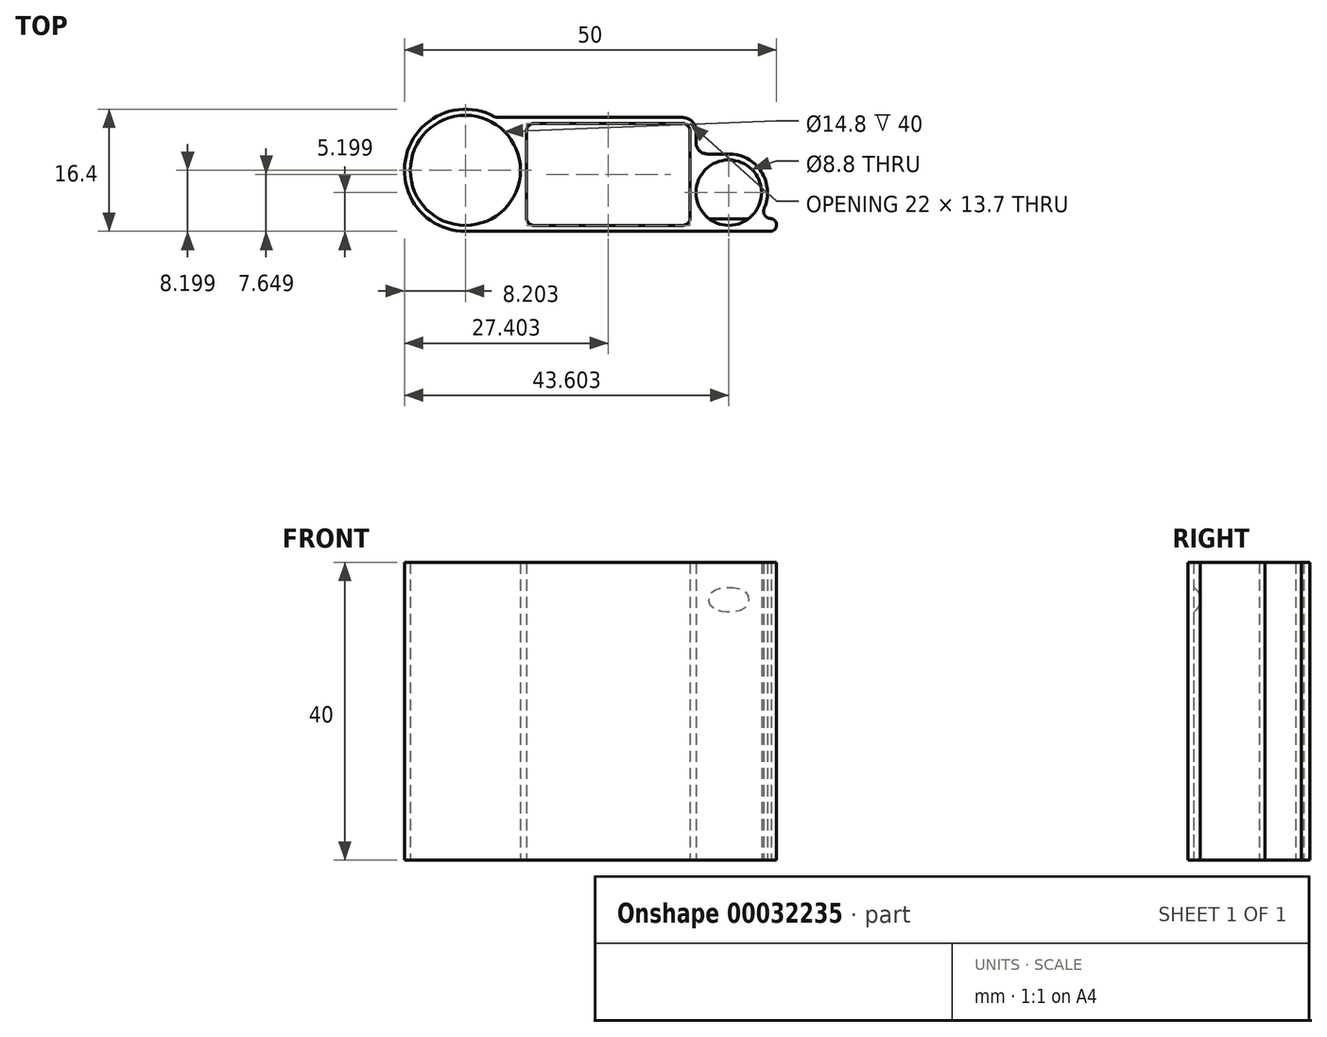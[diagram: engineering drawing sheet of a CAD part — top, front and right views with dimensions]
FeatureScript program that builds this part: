
annotation { "Feature Type Name" : "Feature", "Feature Type Description" : "" }
export const myFeature = defineFeature(function(context is Context, id is Id, definition is map)
    precondition{}
    {
        {
            var Q0;
            Q0=qCreatedBy(makeId("Top.planeOp"),FACE);
            var sketch = newSketch(context, id + "F0", { "sketchPlane" : qUnion([Q0])});
            skCircle(sketch, "E0", {"center": v(-31.66, -11.88) * mm, "radius": 7.4 * mm});
            skLineSegment(sketch, "E1.0", {"start": v(-31.66, -20.08) * mm, "end": v(9.34, -20.08) * mm});
            skArc(sketch, "E2.trimOffspring", {"start": v(-27.77, -4.66) * mm, "mid": v(-39.6, -9.88) * mm, "end": v(-31.66, -20.08) * mm});
            skPoint(sketch, "E3.end.orphan", {"position": v(-39.86, -11.88) * mm});
            skPoint(sketch, "E4.visualSharp", {"position": v(10.14, -20.08) * mm});
            skPoint(sketch, "E5.visualSharp", {"position": v(0.2, -18.37) * mm});
            skLineSegment(sketch, "E6", {"start": v(10.14, -19.17) * mm, "end": v(10.14, -19.28) * mm});
            skArc(sketch, "E7.filletArc", {"start": v(10.14, -19.17) * mm, "mid": v(9.94, -18.64) * mm, "end": v(9.43, -18.38) * mm});
            skArc(sketch, "E8.filletArc", {"start": v(9.34, -20.08) * mm, "mid": v(9.9, -19.85) * mm, "end": v(10.14, -19.28) * mm});
            skLineSegment(sketch, "E9", {"start": v(-23.46, -18.28) * mm, "end": v(-23.46, -6.58) * mm});
            skLineSegment(sketch, "E10", {"start": v(-22.46, -19.28) * mm, "end": v(-2.46, -19.28) * mm});
            skLineSegment(sketch, "E11", {"start": v(-22.46, -5.58) * mm, "end": v(-2.46, -5.58) * mm});
            skLineSegment(sketch, "E12.trimOffspring", {"start": v(-1.46, -6.58) * mm, "end": v(-1.46, -18.28) * mm});
            skCircle(sketch, "E13", {"center": v(3.74, -14.88) * mm, "radius": 4.4 * mm});
            skArc(sketch, "E14", {"start": v(8.5, -16.97) * mm, "mid": v(8.1, -12.04) * mm, "end": v(3.74, -9.68) * mm});
            skPoint(sketch, "E15.visualSharp", {"position": v(-23.82, -9.48) * mm});
            skPoint(sketch, "E16.visualSharp", {"position": v(9.34, -18.37) * mm});
            skPoint(sketch, "E17.visualSharp", {"position": v(7.6, -18.37) * mm});
            skArc(sketch, "E17.filletArc", {"start": v(8.5, -16.97) * mm, "mid": v(8.58, -17.92) * mm, "end": v(9.42, -18.37) * mm});
            skPoint(sketch, "E18.visualSharp", {"position": v(-23.46, -5.58) * mm});
            skArc(sketch, "E18.filletArc", {"start": v(-22.46, -5.58) * mm, "mid": v(-23.16, -5.87) * mm, "end": v(-23.46, -6.58) * mm});
            skPoint(sketch, "E19.visualSharp", {"position": v(-23.46, -19.28) * mm});
            skArc(sketch, "E19.filletArc", {"start": v(-23.46, -18.28) * mm, "mid": v(-23.16, -18.99) * mm, "end": v(-22.46, -19.28) * mm});
            skPoint(sketch, "E20.visualSharp", {"position": v(-1.46, -5.58) * mm});
            skArc(sketch, "E20.filletArc", {"start": v(-1.46, -6.58) * mm, "mid": v(-1.75, -5.87) * mm, "end": v(-2.46, -5.58) * mm});
            skPoint(sketch, "E21.visualSharp", {"position": v(-1.46, -19.28) * mm});
            skArc(sketch, "E21.filletArc", {"start": v(-2.46, -19.28) * mm, "mid": v(-1.75, -18.99) * mm, "end": v(-1.46, -18.28) * mm});
            skLineSegment(sketch, "E22.0", {"start": v(-27.3, -4.78) * mm, "end": v(-2.46, -4.78) * mm});
            skPoint(sketch, "E23.visualSharp", {"position": v(-27.55, -4.78) * mm});
            skArc(sketch, "E23.filletArc", {"start": v(-27.77, -4.66) * mm, "mid": v(-27.54, -4.75) * mm, "end": v(-27.3, -4.78) * mm});
            skArc(sketch, "E24.0", {"start": v(-0.66, -6.58) * mm, "mid": v(-1.18, -5.3) * mm, "end": v(-2.46, -4.78) * mm});
            skLineSegment(sketch, "E25.0", {"start": v(-0.66, -6.58) * mm, "end": v(-0.66, -8.18) * mm});
            skLineSegment(sketch, "E26", {"start": v(3.74, -9.68) * mm, "end": v(0.84, -9.68) * mm});
            skPoint(sketch, "E27.visualSharp", {"position": v(-0.66, -9.68) * mm});
            skArc(sketch, "E27.filletArc", {"start": v(-0.66, -8.18) * mm, "mid": v(-0.22, -9.24) * mm, "end": v(0.84, -9.68) * mm});
            skLineSegment(sketch, "E28", {"start": v(9.42, -18.37) * mm, "end": v(9.43, -18.38) * mm});
            skSolve(sketch);
        }
        {
            var Q0;
            Q0=makeQuery(id+"F0.imprint","IMPRINT",FACE,{"disambiguationData":[TD([[makeQuery(id+"F0.imprint","IMPRINT",EDGE,{"derivedFrom":sQuery(id+"F0.wireOp",EDGE,"E0")}),-1.0]])]});
            var Q1;
            Q1=qSketchRegion(id+"F0",true);
            extrude(context, id + "F1", {"entities" : qUnion([Q0, Q1]), "depth" : 40 * mm});
        }
        {
            var Q0;
            Q0=qCreatedBy(makeId("Right.planeOp"),FACE);
            cPlane(context, id + "F2", {"entities" : qUnion([Q0]), "cplaneType" : CPlaneType.OFFSET, "offset" : 7 * mm, "width" : 150 * mm, "height" : 150 * mm});
        }
        {
            var Q0;
            Q0=qCreatedBy(id+"F2.planeOp",FACE);
            var sketch = newSketch(context, id + "F3", { "sketchPlane" : qUnion([Q0])});
            skArc(sketch, "E29", {"start": v(-19.58, 33.17) * mm, "mid": v(-18.38, 35) * mm, "end": v(-19.58, 36.83) * mm});
            skLineSegment(sketch, "E30", {"start": v(-20.38, 35) * mm, "end": v(-18.38, 35) * mm});
            skLineSegment(sketch, "E31", {"start": v(-19.58, 36.83) * mm, "end": v(-19.58, 33.17) * mm});
            skSolve(sketch);
        }
        {
            var Q0;
            Q0=qSketchRegion(id+"F3",true);
            extrude(context, id + "F4", {"entities" : qUnion([Q0]), "operationType" : NewBodyOperationType.ADD, "oppositeDirection" : true, "depth" : 8 * mm});
        }
    });
